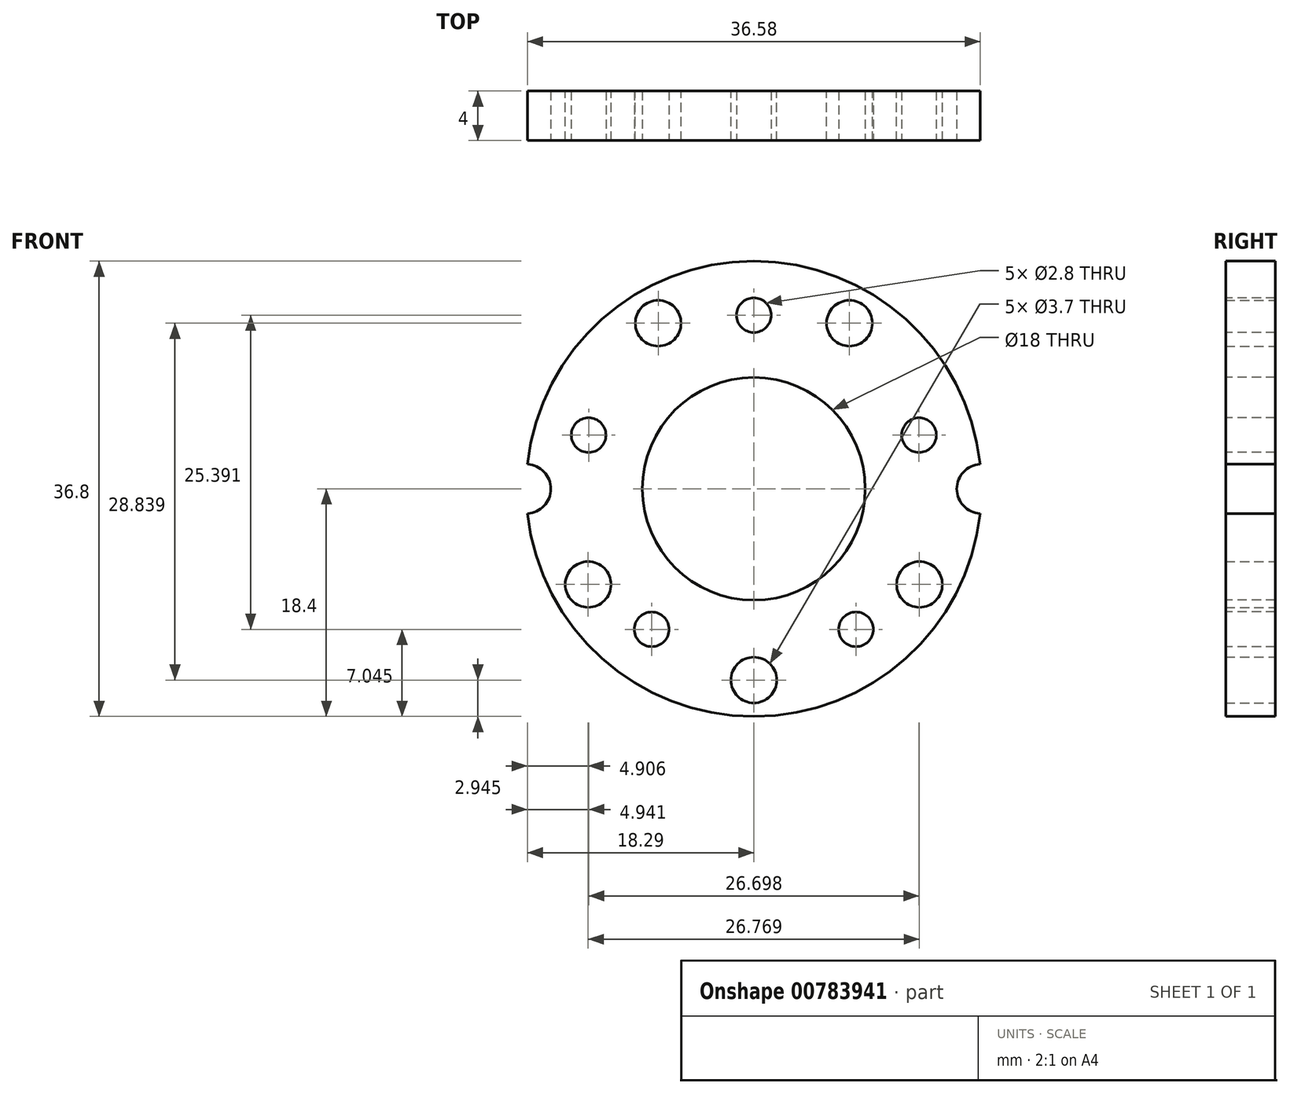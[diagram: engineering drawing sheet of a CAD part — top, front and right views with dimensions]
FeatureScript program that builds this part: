
annotation { "Feature Type Name" : "Feature", "Feature Type Description" : "" }
export const myFeature = defineFeature(function(context is Context, id is Id, definition is map)
    precondition{}
    {
        {
            var Q0;
            Q0=qCreatedBy(makeId("Front.planeOp"),FACE);
            var sketch = newSketch(context, id + "F0", { "sketchPlane" : qUnion([Q0])});
            skCircle(sketch, "E0", {"center": v(0, 0) * mm, "radius": 18.4 * mm});
            skCircle(sketch, "E1", {"center": v(0, 0) * mm, "radius": 9 * mm});
            skCircle(sketch, "E2.cCircle", {"center": v(0, 0) * mm, "radius": 14.04 * mm, "construction": true});
            skLineSegment(sketch, "E2.0", {"start": v(0, 14.04) * mm, "end": v(13.35, 4.34) * mm, "construction": true});
            skLineSegment(sketch, "E2.1", {"start": v(13.35, 4.34) * mm, "end": v(8.25, -11.36) * mm, "construction": true});
            skLineSegment(sketch, "E2.2", {"start": v(8.25, -11.36) * mm, "end": v(-8.25, -11.36) * mm, "construction": true});
            skLineSegment(sketch, "E2.3", {"start": v(-8.25, -11.36) * mm, "end": v(-13.35, 4.34) * mm, "construction": true});
            skLineSegment(sketch, "E2.4", {"start": v(-13.35, 4.34) * mm, "end": v(0, 14.04) * mm, "construction": true});
            skCircle(sketch, "E3", {"center": v(0, 14.04) * mm, "radius": 1.4 * mm});
            skCircle(sketch, "E4", {"center": v(13.35, 4.34) * mm, "radius": 1.4 * mm});
            skCircle(sketch, "E5", {"center": v(8.25, -11.36) * mm, "radius": 1.4 * mm});
            skCircle(sketch, "E6", {"center": v(-8.25, -11.36) * mm, "radius": 1.4 * mm});
            skCircle(sketch, "E7", {"center": v(-13.35, 4.34) * mm, "radius": 1.4 * mm});
            skSolve(sketch);
        }
        {
            var Q0;
            Q0=makeQuery(id+"F0.imprint","IMPRINT",FACE,{"disambiguationData":[TD([[makeQuery(id+"F0.imprint","IMPRINT",EDGE,{"derivedFrom":sQuery(id+"F0.wireOp",EDGE,"E0")}),1.0]])]});
            extrude(context, id + "F1", {"entities" : qUnion([Q0]), "oppositeDirection" : true, "depth" : 4 * mm, "offsetDistance" : 25 * mm});
        }
        {
            var Q0;
            Q0=makeQuery(id+"F1.opExtrude","CAP_FACE",FACE,{"disambiguationData":[OSD([sQuery(id+"F0.wireOp",EDGE,"E0"),sQuery(id+"F0.wireOp",EDGE,"E1"),sQuery(id+"F0.wireOp",EDGE,"E3"),sQuery(id+"F0.wireOp",EDGE,"E4"),sQuery(id+"F0.wireOp",EDGE,"E5"),sQuery(id+"F0.wireOp",EDGE,"E6"),sQuery(id+"F0.wireOp",EDGE,"E7")])],"isStart":false});
            var sketch = newSketch(context, id + "F2", { "sketchPlane" : qUnion([Q0])});
            skCircle(sketch, "E8.cCircle", {"center": v(0, 0) * mm, "radius": 15.45 * mm, "construction": true});
            skLineSegment(sketch, "E8.0", {"start": v(13.38, -7.73) * mm, "end": v(7.73, -13.38) * mm, "construction": true});
            skLineSegment(sketch, "E8.1", {"start": v(7.73, -13.38) * mm, "end": v(0, -15.45) * mm, "construction": true});
            skLineSegment(sketch, "E8.2", {"start": v(0, -15.45) * mm, "end": v(-7.73, -13.38) * mm, "construction": true});
            skLineSegment(sketch, "E8.3", {"start": v(-7.73, -13.38) * mm, "end": v(-13.38, -7.73) * mm, "construction": true});
            skLineSegment(sketch, "E8.4", {"start": v(-13.38, -7.73) * mm, "end": v(-15.45, 0) * mm, "construction": true});
            skLineSegment(sketch, "E8.5", {"start": v(-15.45, 0) * mm, "end": v(-13.38, 7.73) * mm, "construction": true});
            skLineSegment(sketch, "E8.6", {"start": v(-13.38, 7.73) * mm, "end": v(-7.73, 13.38) * mm, "construction": true});
            skLineSegment(sketch, "E8.7", {"start": v(-7.73, 13.38) * mm, "end": v(0, 15.45) * mm, "construction": true});
            skLineSegment(sketch, "E8.8", {"start": v(0, 15.45) * mm, "end": v(7.73, 13.38) * mm, "construction": true});
            skLineSegment(sketch, "E8.9", {"start": v(7.73, 13.38) * mm, "end": v(13.38, 7.73) * mm, "construction": true});
            skLineSegment(sketch, "E8.10", {"start": v(13.38, 7.73) * mm, "end": v(15.45, 0) * mm, "construction": true});
            skLineSegment(sketch, "E8.11", {"start": v(15.45, 0) * mm, "end": v(13.38, -7.73) * mm, "construction": true});
            skCircle(sketch, "E9", {"center": v(-13.38, 7.73) * mm, "radius": 1.85 * mm, "construction": true});
            skCircle(sketch, "E10", {"center": v(0, -15.45) * mm, "radius": 1.85 * mm});
            skCircle(sketch, "E11", {"center": v(13.38, 7.73) * mm, "radius": 1.85 * mm, "construction": true});
            skCircle(sketch, "E12", {"center": v(13.38, -7.73) * mm, "radius": 1.85 * mm});
            skCircle(sketch, "E13", {"center": v(-13.38, -7.73) * mm, "radius": 1.85 * mm});
            skCircle(sketch, "E14", {"center": v(-7.73, 13.38) * mm, "radius": 1.85 * mm});
            skCircle(sketch, "E15", {"center": v(7.73, 13.38) * mm, "radius": 1.85 * mm});
            skSolve(sketch);
        }
        {
            var Q0;
            Q0 = qSketchRegion(id + "F2", true);
            extrude(context, id + "F3", {"entities" : qUnion([Q0]), "operationType" : NewBodyOperationType.REMOVE, "oppositeDirection" : true, "depth" : 25 * mm, "offsetDistance" : 25 * mm});
        }
        {
            var Q0;
            Q0=makeQuery(id+"F1.opExtrude","CAP_FACE",FACE,{"disambiguationData":[OSD([sQuery(id+"F0.wireOp",EDGE,"E0"),sQuery(id+"F0.wireOp",EDGE,"E1"),sQuery(id+"F0.wireOp",EDGE,"E3"),sQuery(id+"F0.wireOp",EDGE,"E4"),sQuery(id+"F0.wireOp",EDGE,"E5"),sQuery(id+"F0.wireOp",EDGE,"E6"),sQuery(id+"F0.wireOp",EDGE,"E7")])],"isStart":true});
            var sketch = newSketch(context, id + "F4", { "sketchPlane" : qUnion([Q0])});
            skCircle(sketch, "E16", {"center": v(-18.4, 0) * mm, "radius": 2 * mm});
            skCircle(sketch, "E17", {"center": v(18.4, 0) * mm, "radius": 2 * mm});
            skLineSegment(sketch, "E18", {"start": v(-18.4, 0) * mm, "end": v(18.4, 0) * mm, "construction": true});
            skSolve(sketch);
        }
        {
            var Q0;
            {var subQ0=sQuery(id+"F4.wireOp",EDGE,"E16");var subQ1=makeQuery(id+"F1.opExtrude","CAP_EDGE",EDGE,{"disambiguationData":[OSD([sQuery(id+"F0.wireOp",EDGE,"E0")])],"isStart":true});var subQ2=makeQuery(id+"F4.imprint","INTERSECT",VERTEX,{"disambiguationData":[OD(0.0)],"derivedFrom":[subQ1,subQ0]});Q0=makeQuery(id+"F4.imprint","IMPRINT",FACE,{"disambiguationData":[TD([[makeQuery(id+"F4.imprint","IMPRINT",EDGE,{"disambiguationData":[TD([[subQ2,-1.0]])],"derivedFrom":subQ0}),1.0]])]});}
            var Q1;
            {var subQ0=sQuery(id+"F4.wireOp",EDGE,"E17");var subQ1=makeQuery(id+"F1.opExtrude","CAP_EDGE",EDGE,{"disambiguationData":[OSD([sQuery(id+"F0.wireOp",EDGE,"E0")])],"isStart":true});var subQ2=makeQuery(id+"F4.imprint","INTERSECT",VERTEX,{"disambiguationData":[OD(0.0)],"derivedFrom":[subQ1,subQ0]});Q1=makeQuery(id+"F4.imprint","IMPRINT",FACE,{"disambiguationData":[TD([[makeQuery(id+"F4.imprint","IMPRINT",EDGE,{"disambiguationData":[TD([[subQ2,1.0]])],"derivedFrom":subQ0}),1.0]])]});}
            extrude(context, id + "F5", {"entities" : qUnion([Q0, Q1]), "operationType" : NewBodyOperationType.REMOVE, "oppositeDirection" : true, "depth" : 25 * mm, "offsetDistance" : 25 * mm});
        }
    });
